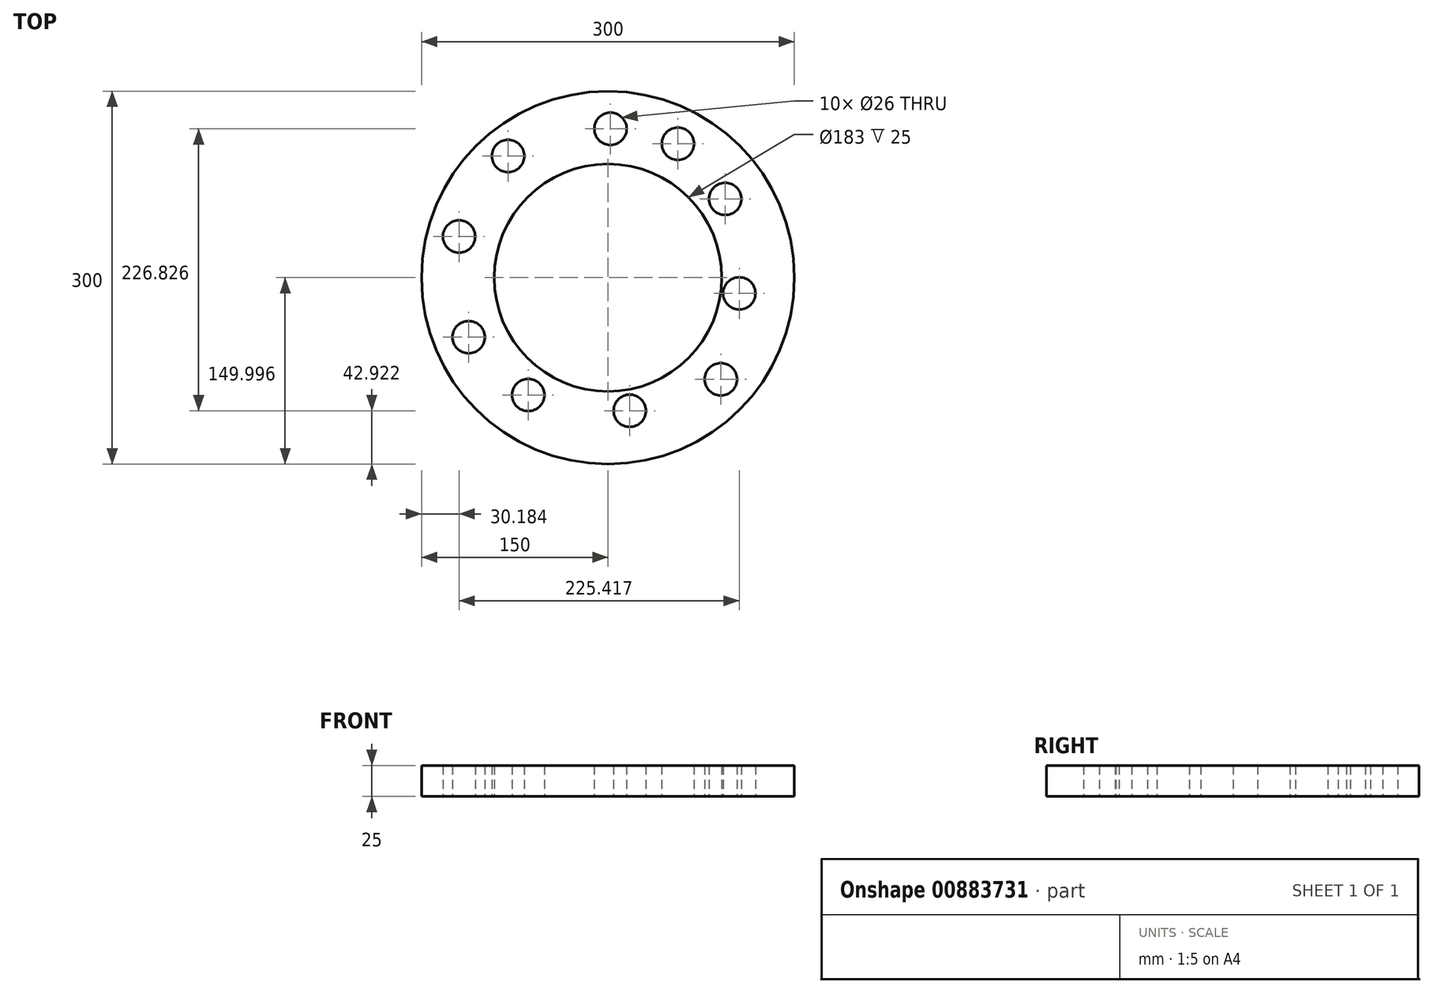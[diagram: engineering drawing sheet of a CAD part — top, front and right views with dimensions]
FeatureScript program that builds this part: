
annotation { "Feature Type Name" : "Feature", "Feature Type Description" : "" }
export const myFeature = defineFeature(function(context is Context, id is Id, definition is map)
    precondition{}
    {
        {
            var Q0;
            Q0=qCreatedBy(makeId("Top.planeOp"),FACE);
            var sketch = newSketch(context, id + "F0", { "sketchPlane" : qUnion([Q0])});
            skCircle(sketch, "E0", {"center": v(-15.28, 11.64) * mm, "radius": 150 * mm});
            skCircle(sketch, "E1", {"center": v(-15.28, 11.64) * mm, "radius": 91.5 * mm});
            skCircle(sketch, "E2", {"center": v(-13.23, 131.39) * mm, "radius": 13 * mm});
            skCircle(sketch, "E3", {"center": v(41.01, 119.41) * mm, "radius": 13 * mm});
            skCircle(sketch, "E4", {"center": v(79.05, 75.03) * mm, "radius": 13 * mm});
            skCircle(sketch, "E5", {"center": v(90.32, -1.05) * mm, "radius": 13 * mm});
            skCircle(sketch, "E6", {"center": v(75.53, -70.08) * mm, "radius": 13 * mm});
            skCircle(sketch, "E7", {"center": v(2.27, -95.44) * mm, "radius": 13 * mm});
            skCircle(sketch, "E8", {"center": v(-79.45, -82.76) * mm, "radius": 13 * mm});
            skCircle(sketch, "E9", {"center": v(-127.35, -36.27) * mm, "radius": 13 * mm});
            skCircle(sketch, "E10", {"center": v(-135.1, 44.74) * mm, "radius": 13 * mm});
            skCircle(sketch, "E11", {"center": v(-95.65, 109.55) * mm, "radius": 13 * mm});
            skSolve(sketch);
        }
        {
            var Q0;
            Q0 = qSketchRegion(id + "F0", true);
            extrude(context, id + "F1", {"entities" : qUnion([Q0]), "depth" : 25 * mm, "offsetDistance" : 25 * mm});
        }
    });
